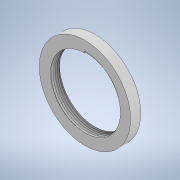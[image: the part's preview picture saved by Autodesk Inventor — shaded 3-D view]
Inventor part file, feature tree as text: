
AUTODESK INVENTOR PART (.ipt)
format: ipt  version: 2022.2 (Build 262287030, 287C)  size: 320,000 bytes
history: native  units: in
note: dims shown in document units (in); Inventor stores cm internally (conversion verified against a paired STEP export)
features: sketch x2, extrude x1, helix x1
ambient origin geometry x8: Origin, YZ Plane, XZ Plane, XY Plane, X Axis, Y Axis, Z Axis, Center Point
bodies: Solid1 (feature_tree)
feature tree (4):
  extrude  "Extrusion1"  Depth=0.1969in
  helix  "Coil1"  [1 undecoded]
  sketch  "Sketch1"  dims[d0=1.3358in d1=1.7717in d2=0.1969in d3=0.0in]
  sketch  "Sketch2"  dims[d4=0.0401in d5=0.0394in d6=0.6679in d7=0.0039in d8=0.0in d9=0.0394in d10=0.3937in d11=3.1496in d12=0.0in d13=90.0deg d14=90.0deg d15=0.0in d16=0.0in]
note: 1 required parameter value undecoded (feature->parameter linkage not recoverable at this tier; creation-order binding heuristic only, values carry confidence <= 0.55)
